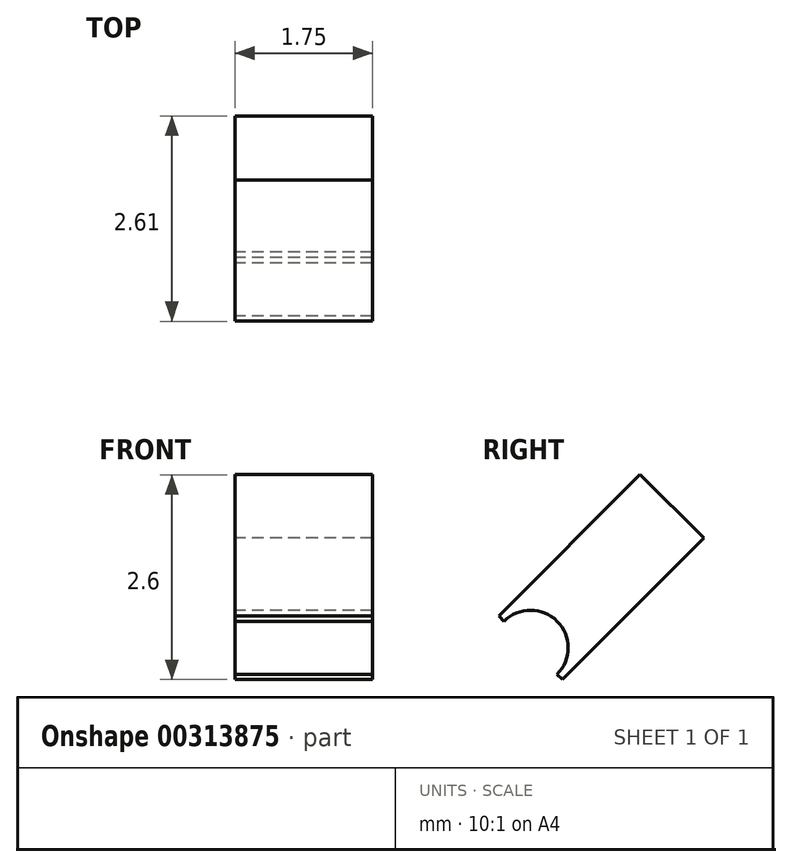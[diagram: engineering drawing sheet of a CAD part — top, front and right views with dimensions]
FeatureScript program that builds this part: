
annotation { "Feature Type Name" : "Feature", "Feature Type Description" : "" }
export const myFeature = defineFeature(function(context is Context, id is Id, definition is map)
    precondition{}
    {
        {
            var Q0;
            Q0=qCreatedBy(makeId("Right.planeOp"),FACE);
            var sketch = newSketch(context, id + "F0", { "sketchPlane" : qUnion([Q0])});
            skLineSegment(sketch, "E0.bottom", {"start": v(0, 0) * mm, "end": v(2.54, 0) * mm});
            skLineSegment(sketch, "E0.top", {"start": v(0, 1.14) * mm, "end": v(2.54, 1.14) * mm});
            skLineSegment(sketch, "E0.left", {"start": v(0, 0) * mm, "end": v(0, 1.14) * mm});
            skLineSegment(sketch, "E0.right", {"start": v(2.54, 0) * mm, "end": v(2.54, 1.14) * mm});
            skLineSegment(sketch, "E1", {"start": v(0, 1.14) * mm, "end": v(0, 0.57) * mm});
            skCircle(sketch, "E2", {"center": v(0, 0.57) * mm, "radius": 0.48 * mm});
            skSolve(sketch);
        }
        {
            var Q0;
            {var subQ1=sQuery(id+"F0.wireOp",EDGE,"E0.bottom");Q0=makeQuery(id+"F0.imprint","IMPRINT",FACE,{"disambiguationData":[TD([[makeQuery(id+"F0.imprint","IMPRINT",EDGE,{"derivedFrom":subQ1}),1.0]])]});}
            extrude(context, id + "F1", {"entities" : qUnion([Q0]), "depth" : 1.75 * mm});
        }
        {
            var Q0;
            Q0=makeQuery(id+"F1.opExtrude","SWEPT_BODY",BODY,{"disambiguationData":[OSD([sQuery(id+"F0.wireOp",EDGE,"E0.bottom"),sQuery(id+"F0.wireOp",EDGE,"E0.top"),sQuery(id+"F0.wireOp",EDGE,"E0.left"),sQuery(id+"F0.wireOp",EDGE,"E0.right"),sQuery(id+"F0.wireOp",EDGE,"E1"),sQuery(id+"F0.wireOp",EDGE,"E2")])]});
            var Q1;
            Q1=makeQuery(id+"F1.opExtrude","SWEPT_EDGE",EDGE,{"disambiguationData":[OSD([sQuery(id+"F0.wireOp",EDGE,"E0.bottom"),sQuery(id+"F0.wireOp",EDGE,"E0.left")])]});
            transform(context, id + "F2", {"entities" : qUnion([Q0]), "transformType" : TransformType.ROTATION, "transformAxis" : qUnion([Q1]), "angle" : 45 * degree, "oppositeDirection" : true, "makeCopy" : false});
        }
    });
